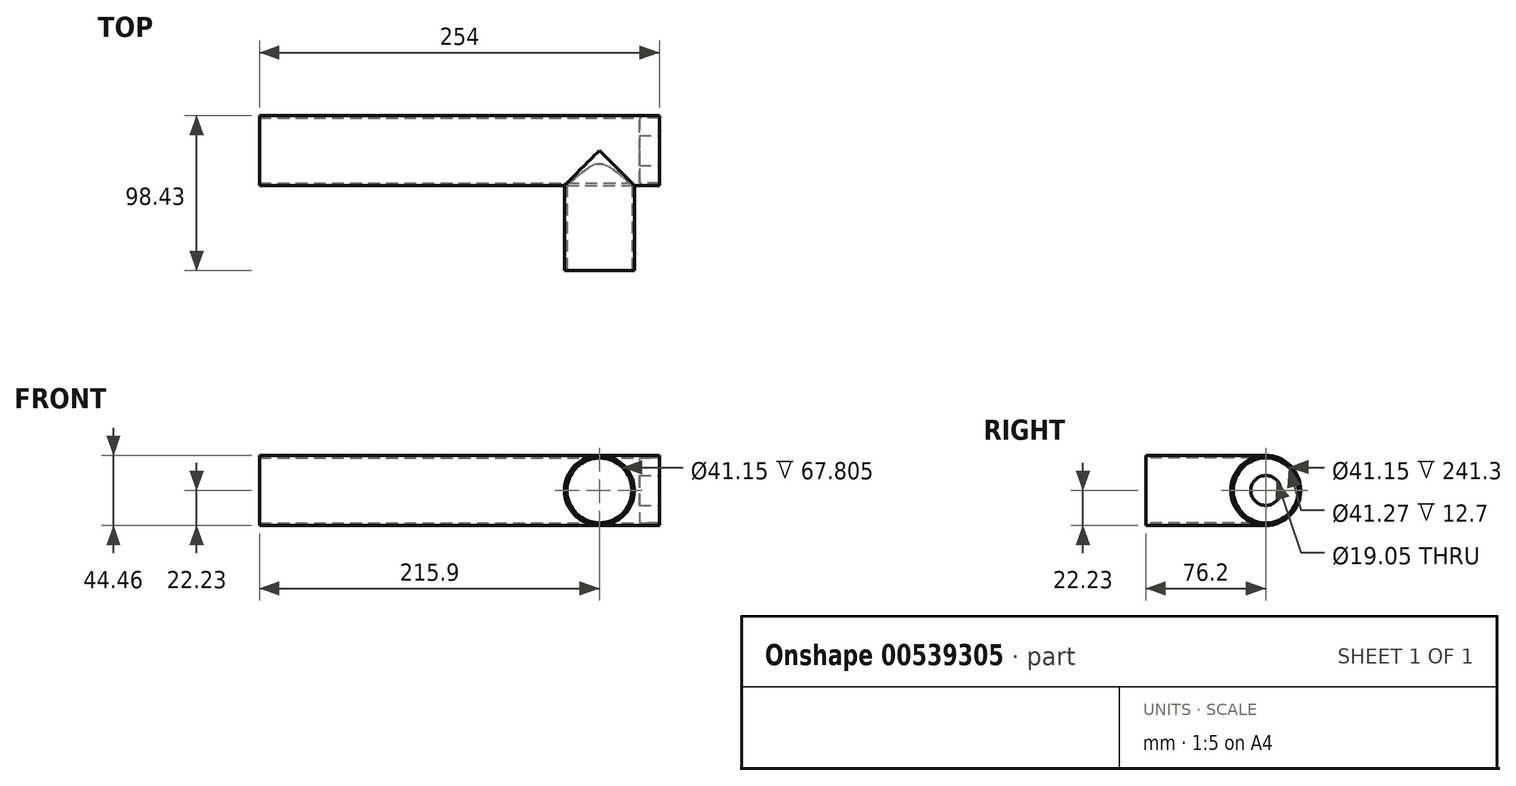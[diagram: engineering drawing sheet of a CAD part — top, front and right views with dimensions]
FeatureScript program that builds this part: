
annotation { "Feature Type Name" : "Feature", "Feature Type Description" : "" }
export const myFeature = defineFeature(function(context is Context, id is Id, definition is map)
    precondition{}
    {
        {
            var Q0;
            Q0=qCreatedBy(makeId("Right.planeOp"),FACE);
            var sketch = newSketch(context, id + "F0", { "sketchPlane" : qUnion([Q0])});
            skCircle(sketch, "E0", {"center": v(0, 0) * mm, "radius": 22.23 * mm});
            skCircle(sketch, "E1", {"center": v(0, 0) * mm, "radius": 20.57 * mm});
            skSolve(sketch);
        }
        {
            var Q0;
            Q0=makeQuery(id+"F0.imprint","IMPRINT",FACE,{"disambiguationData":[TD([[makeQuery(id+"F0.imprint","IMPRINT",EDGE,{"derivedFrom":sQuery(id+"F0.wireOp",EDGE,"E0")}),1.0]])]});
            extrude(context, id + "F1", {"entities" : qUnion([Q0]), "oppositeDirection" : true, "depth" : 254 * mm, "offsetDistance" : 25.4 * mm});
        }
        {
            var Q0;
            Q0=qCreatedBy(makeId("Front.planeOp"),FACE);
            var sketch = newSketch(context, id + "F2", { "sketchPlane" : qUnion([Q0])});
            skLineSegment(sketch, "E2.bottom", {"start": v(0, 0) * mm, "end": v(-12.7, 0) * mm});
            skLineSegment(sketch, "E2.top", {"start": v(0, 20.64) * mm, "end": v(-12.7, 20.64) * mm});
            skLineSegment(sketch, "E2.left", {"start": v(0, 0) * mm, "end": v(0, 20.64) * mm});
            skLineSegment(sketch, "E2.right", {"start": v(-12.7, 0) * mm, "end": v(-12.7, 20.64) * mm});
            skSolve(sketch);
        }
        {
            var Q0;
            Q0=makeQuery(id+"F2.imprint","IMPRINT",FACE,{"disambiguationData":[TD([[makeQuery(id+"F2.imprint","IMPRINT",EDGE,{"derivedFrom":sQuery(id+"F2.wireOp",EDGE,"E2.bottom")}),-1.0]])]});
            var Q1;
            Q1=sQuery(id+"F2.wireOp",EDGE,"E2.bottom");
            revolve(context, id + "F3", {"operationType" : NewBodyOperationType.REMOVE, "entities" : qUnion([Q0]), "axis" : qUnion([Q1]), "revolveType" : RevolveType.FULL, "oppositeDirection" : true});
        }
        {
            var Q0;
            Q0=qCreatedBy(makeId("Front.planeOp"),FACE);
            var sketch = newSketch(context, id + "F4", { "sketchPlane" : qUnion([Q0])});
            skLineSegment(sketch, "E3.bottom", {"start": v(0, 9.53) * mm, "end": v(-12.7, 9.52) * mm});
            skLineSegment(sketch, "E3.top", {"start": v(0, 20.64) * mm, "end": v(-12.7, 20.64) * mm});
            skLineSegment(sketch, "E3.left", {"start": v(0, 9.53) * mm, "end": v(0, 20.64) * mm});
            skLineSegment(sketch, "E3.right", {"start": v(-12.7, 9.52) * mm, "end": v(-12.7, 20.64) * mm});
            skLineSegment(sketch, "E4", {"start": v(0, 0) * mm, "end": v(-16.03, 0) * mm, "construction": true});
            skSolve(sketch);
        }
        {
            var Q0;
            Q0=makeQuery(id+"F4.imprint","IMPRINT",FACE,{"disambiguationData":[TD([[makeQuery(id+"F4.imprint","IMPRINT",EDGE,{"derivedFrom":sQuery(id+"F4.wireOp",EDGE,"E3.bottom")}),-1.0]])]});
            var Q1;
            Q1=sQuery(id+"F4.wireOp",EDGE,"E4");
            revolve(context, id + "F5", {"entities" : qUnion([Q0]), "axis" : qUnion([Q1]), "revolveType" : RevolveType.FULL});
        }
        {
            var Q0;
            Q0=qCreatedBy(makeId("Front.planeOp"),FACE);
            cPlane(context, id + "F6", {"entities" : qUnion([Q0]), "cplaneType" : CPlaneType.OFFSET, "offset" : 76.2 * mm, "width" : 152.4 * mm, "height" : 152.4 * mm});
        }
        {
            var Q0;
            Q0=qCreatedBy(id+"F6.planeOp",FACE);
            var sketch = newSketch(context, id + "F7", { "sketchPlane" : qUnion([Q0])});
            skLineSegment(sketch, "E5", {"start": v(0, 0) * mm, "end": v(-38.1, 0) * mm, "construction": true});
            skCircle(sketch, "E6", {"center": v(-38.1, 0) * mm, "radius": 22.23 * mm});
            skCircle(sketch, "E7", {"center": v(-38.1, 0) * mm, "radius": 20.57 * mm});
            skSolve(sketch);
        }
        {
            var Q0;
            Q0=makeQuery(id+"F7.imprint","IMPRINT",FACE,{"disambiguationData":[TD([[makeQuery(id+"F7.imprint","IMPRINT",EDGE,{"derivedFrom":sQuery(id+"F7.wireOp",EDGE,"E6")}),1.0]])]});
            extrude(context, id + "F8", {"entities" : qUnion([Q0]), "operationType" : NewBodyOperationType.ADD, "endBound" : BoundingType.UP_TO_NEXT, "oppositeDirection" : true, "depth" : 25.4 * mm, "offsetDistance" : 25.4 * mm});
        }
    });
